# Revit family: msz-gv2256_23_60hz
name_source: partatom
category: 機械設備
units: mm (PartAtom-declared; Revit-internal decimal feet)

## family parameters
OmniClass タイトル = Split System Air Conditioning Units
OmniClass 番号 = 23.75.10.24.21.27.27
パーツ タイプ = 標準
ロード時にボイドで切り取り = いいえ
丸型コネクタ寸法 = 直径を使用
作業面ベース = いいえ
共有 = いいえ
常に垂直 = はい
部屋計算ポイント = いいえ

## types (12) — shared parameters
Clearance Bottom = 7  [stored 0.0229659 ft]
Clearance Left = 20  [stored 0.0656168 ft]
Clearance Right = 40  [stored 0.131234 ft]
Clearance Top = 33  [stored 0.108268 ft]
Depth = 225  [stored 0.738189 ft]
FamilyVersion = v1.7
Height = 295  [stored 0.967848 ft]
IfcExportAs = IfcUnitaryEquipmentType
IfcExportType = AIRCONDITIONINGUNIT
OmniClassCode = 23-33 17 13 11
URL = https://www.mitsubishielectric.co.jp
Uniclass2015Code = Pr_70_65_03_84
Uniclass2015Title = Split coil remote air cooled condensing units
Uniclass2015Version = Systems v1.9
Width = 799  [stored 2.62139 ft]
ケーブルサイズ1 = 2 mm
ケーブル種類1 = VVF
サービススペース = はい
ドレン管径 = 16.00 mm
ドレン管高さ = 190
仕様書バージョン = Version1.0
企業コード = 108420
冷媒ガス管径 = 9.52 mm
冷媒ガス管長さ = 86  [stored 0.282152 ft]
冷媒ガス管高さ = 126  [stored 0.413386 ft]
冷媒液管径 = 6.35 mm
冷媒液管長さ = 85  [stored 0.278871 ft]
冷媒液管高さ = 126  [stored 0.413386 ft]
冷媒管径 = 100.00 mm
冷媒管径符号 = Ab
冷媒高低圧ガス管径 = 0.00 mm
分類コード = 50053004203000
加湿給水管径 = 0.00 mm
参照している仕様書等のバージョン = 公共建築物標準仕様書（機械設備工事編）平成31年度版
周波数 = 60 Hz
呼称 = パッケージ形空気調和機_室内機
始動方式 = 直入
形式 = 壁掛（露出）形
推奨ブレーカー容量 = 15 A
本体マテリアル = <カテゴリ別>
極数 = 1
法定耐用年数 = 6
発停方法 = 付属スイッチ
相 = 1
相_電気ヒーター = 1
積算_科目 = 1 空気調和設備
符号 = ACR-WR
製品リリース年月 = -
製品出荷対象 = 国内
製造元 = 三菱電機株式会社
設置方法 = 壁掛 (露出)形
説明 = ルームエアコン(霧ヶ峰) 　GVシリーズ　室内ユニット
負荷分類 = 10_ファンコイル類
運転質量 = 0.00 kg
電圧_電気ヒーター = 0 V
zero-valued in all types: APF, COP, Clearance Back

## per-type parameters (varying)
| type | Clearance Front | MAX風量 | モデル | 冷房 風量 | 冷房能力 | 暖房 風量 | 暖房能力 | 消費電力 | 消費電力_冷房 | 消費電力_暖房 | 製品質量 | 質量 | 運転音(中冷房)  db | 運転音(中暖房)  db | 運転音(弱冷房)  db | 運転音(弱暖房)  db | 運転音(強冷房)  db | 運転音(強暖房)  db | 運転音(静冷房)  db | 電動機出力_送風機 | 電圧 | 音響パワーレベル(dB) | 風量 |
| 壁掛_MSZ-GV2223-W-IN | 445  [stored 1.45997 ft] | 635.0 m³/h | MSZ-GV22**-*-IN | 635.0 m³/h | 2.2 kW | 635.0 m³/h | 2.20 kW | 655.00 W | 655.00 W | 470.00 W | 8.00 kg | 9.60 kg | 51 | 50 | 43 | 43 | 62 | 64 | 41 | 28.00 W | 100 V | 64 | 635.0 m³/h |
| 壁掛_MSZ-GV2523-W-IN | 445  [stored 1.45997 ft] | 655.0 m³/h | MSZ-GV25**-*-IN | 635.0 m³/h | 2.5 kW | 635.0 m³/h | 2.80 kW | 745.00 W | 745.00 W | 625.00 W | 8.00 kg | 9.60 kg | 51 | 50 | 43 | 43 | 63 | 64 | 41 | 28.00 W | 100 V | 64 | 655.0 m³/h |
| 壁掛_MSZ-GV2823-W-IN | 445  [stored 1.45997 ft] | 665.0 m³/h | MSZ-GV28**-*-IN | 665.0 m³/h | 2.8 kW | 650.0 m³/h | 3.60 kW | 910.00 W | 800.00 W | 910.00 W | 9.00 kg | 10.80 kg | 51 | 50 | 43 | 43 | 63 | 64 | 41 | 28.00 W | 100 V | 64 | 665.0 m³/h |
| 壁掛_MSZ-GV3623-W-IN | 445  [stored 1.45997 ft] | 670.0 m³/h | MSZ-GV36**-*-IN | 670.0 m³/h | 3.6 kW | 660.0 m³/h | 4.20 kW | 1415.00 W | 1415.00 W | 1215.00 W | 9.00 kg | 10.80 kg | 54 | 53 | 47 | 47 | 64 | 64 | 41 | 28.00 W | 100 V | 64 | 670.0 m³/h |
| 壁掛_MSZ-GV4023S-W-IN | 445  [stored 1.45997 ft] | 670.0 m³/h | MSZ-GV40**S-*-IN | 670.0 m³/h | 4 kW | 660.0 m³/h | 5.00 kW | 1660.00 W | 1660.00 W | 1480.00 W | 9.00 kg | 10.80 kg | 54 | 54 | 47 | 47 | 66 | 65 | 44 | 40.00 W | 200 V | 66 | 670.0 m³/h |
| 壁掛_MSZ-GV5623S-W-IN | 215  [stored 0.705381 ft] | 785.0 m³/h | MSZ-GV56**S-*-IN | 785.0 m³/h | 5.6 kW | 725.0 m³/h | 6.70 kW | 2380.00 W | 2380.00 W | 1980.00 W | 9.00 kg | 10.80 kg | 54 | 54 | 47 | 47 | 66 | 67 | 45 | 40.00 W | 200 V | 67 | 785.0 m³/h |
| 壁掛_MSZ-GV2223-T-IN | 445  [stored 1.45997 ft] | 635.0 m³/h | MSZ-GV22**-*-IN | 635.0 m³/h | 2.2 kW | 635.0 m³/h | 2.20 kW | 655.00 W | 655.00 W | 470.00 W | 8.00 kg | 9.60 kg | 51 | 50 | 43 | 43 | 62 | 64 | 41 | 28.00 W | 100 V | 64 | 635.0 m³/h |
| 壁掛_MSZ-GV2523-T-IN | 445  [stored 1.45997 ft] | 655.0 m³/h | MSZ-GV25**-*-IN | 635.0 m³/h | 2.5 kW | 635.0 m³/h | 2.80 kW | 745.00 W | 745.00 W | 625.00 W | 8.00 kg | 9.60 kg | 51 | 50 | 43 | 43 | 63 | 64 | 41 | 28.00 W | 100 V | 64 | 655.0 m³/h |
| 壁掛_MSZ-GV2823-T-IN | 445  [stored 1.45997 ft] | 665.0 m³/h | MSZ-GV28**-*-IN | 665.0 m³/h | 2.8 kW | 650.0 m³/h | 3.60 kW | 910.00 W | 800.00 W | 910.00 W | 9.00 kg | 10.80 kg | 51 | 50 | 43 | 43 | 63 | 64 | 41 | 28.00 W | 100 V | 64 | 665.0 m³/h |
| 壁掛_MSZ-GV3623-T-IN | 445  [stored 1.45997 ft] | 670.0 m³/h | MSZ-GV36**-*-IN | 670.0 m³/h | 3.6 kW | 660.0 m³/h | 4.20 kW | 1415.00 W | 1415.00 W | 1215.00 W | 9.00 kg | 10.80 kg | 54 | 53 | 47 | 47 | 64 | 64 | 41 | 28.00 W | 100 V | 64 | 670.0 m³/h |
| 壁掛_MSZ-GV4023S-T-IN | 445  [stored 1.45997 ft] | 670.0 m³/h | MSZ-GV40**S-*-IN | 670.0 m³/h | 4 kW | 660.0 m³/h | 5.00 kW | 1660.00 W | 1660.00 W | 1480.00 W | 9.00 kg | 10.80 kg | 54 | 54 | 47 | 47 | 66 | 65 | 44 | 40.00 W | 200 V | 66 | 670.0 m³/h |
| 壁掛_MSZ-GV5623S-T-IN | 215  [stored 0.705381 ft] | 785.0 m³/h | MSZ-GV56**S-*-IN | 785.0 m³/h | 5.6 kW | 725.0 m³/h | 6.70 kW | 2380.00 W | 2380.00 W | 1980.00 W | 9.00 kg | 10.80 kg | 54 | 54 | 47 | 47 | 66 | 67 | 45 | 40.00 W | 200 V | 67 | 785.0 m³/h |

note: [stored X ft] marks values corroborated as IEEE doubles in the binary element streams (Revit-internal decimal feet)
